# Revit family: Compatta 600 Unit
name_source: partatom
category: Plumbing Fixtures
units: mm (PartAtom-declared; Revit-internal decimal feet)

## family parameters
Always vertical = Yes
Cut with Voids When Loaded = No
Enable Cutting in Views = No
Host = Wall
Maintain Annotation Orientation = No
OmniClass Number = 23.45.00.00
OmniClass Title = Sanitary, Laundry, and Cleaning Equipment
Part Type = Normal
Room Calculation Point = No
Round Connector Dimension = Use Diameter
Shared = No

## types (1)
- Type 1
    Basin = White Ceramic
    Cabinet = Gloss White
    Default Elevation = 0 mm  [stored 0 ft]
    Depth = 470 mm  [stored 1.54199 ft]
    Height = 530 mm  [stored 1.73885 ft]
    Height to top of basin = 830 mm  [stored 2.7231 ft]
    Waste = Aluminium
    Width = 600 mm  [stored 1.9685 ft]

note: [stored X ft] marks values corroborated as IEEE doubles in the binary element streams (Revit-internal decimal feet)

## geometry (parser evidence)
native form markers: Sweep x4
no freeform markers — native parametric forms only
